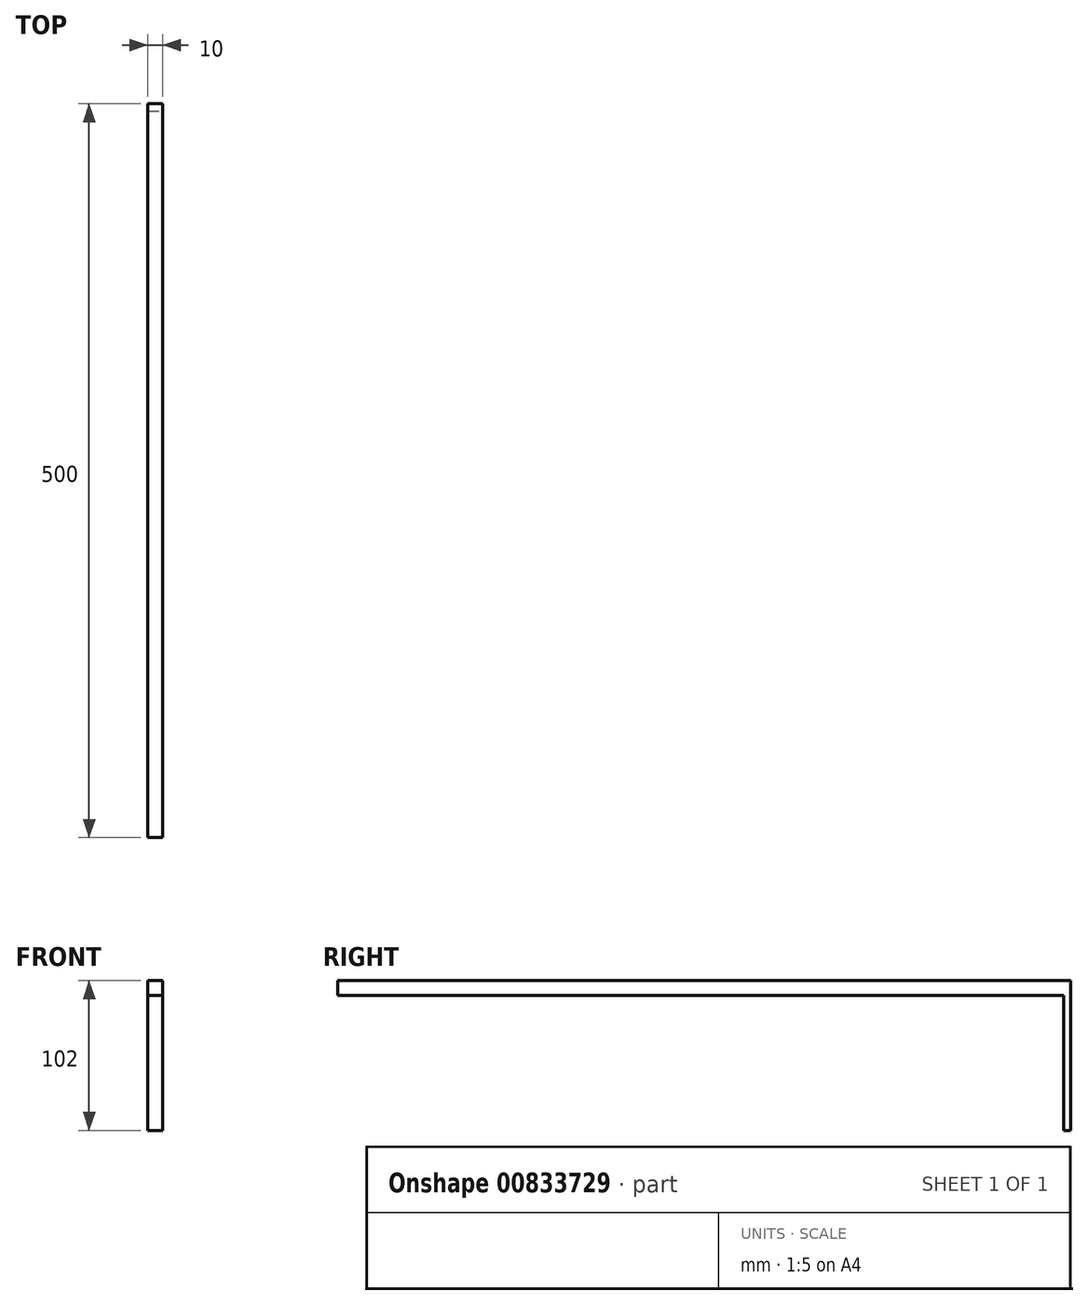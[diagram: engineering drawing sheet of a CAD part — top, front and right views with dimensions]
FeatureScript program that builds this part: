
annotation { "Feature Type Name" : "Feature", "Feature Type Description" : "" }
export const myFeature = defineFeature(function(context is Context, id is Id, definition is map)
    precondition{}
    {
        {
            var Q0;
            Q0=qCreatedBy(makeId("Right.planeOp"),FACE);
            var sketch = newSketch(context, id + "F0", { "sketchPlane" : qUnion([Q0])});
            skLineSegment(sketch, "E0", {"start": v(387.3, 17.23) * mm, "end": v(387.3, -74.77) * mm});
            skLineSegment(sketch, "E1", {"start": v(387.3, 17.23) * mm, "end": v(-112.7, 17.23) * mm});
            skEllipse(sketch, "E2", {"center": v(387.3, 17.23) * mm, "majorRadius": 500 * mm, "minorRadius": 224.74 * mm, "majorAxis": v(-1, 0)});
            skPoint(sketch, "E3.startSnap0", {"position": v(387.3, -207.51) * mm});
            skSolve(sketch);
        }
        {
            var Q0;
            Q0=sQuery(id+"F0.wireOp",EDGE,"E0");
            extrude(context, id + "F1", {"bodyType" : ToolBodyType.SURFACE, "surfaceEntities" : qUnion([Q0]), "depth" : 10 * mm, "offsetDistance" : 25 * mm});
        }
        {
            var Q0;
            Q0=makeQuery(id+"F1.opExtrude","SWEPT_FACE",FACE,{"disambiguationData":[OSD([sQuery(id+"F0.wireOp",EDGE,"E0")])]});
            extrude(context, id + "F2", {"entities" : qUnion([Q0]), "depth" : 5 * mm, "offsetDistance" : 25 * mm});
        }
        {
            var Q0;
            Q0=sQuery(id+"F0.wireOp",EDGE,"E1");
            extrude(context, id + "F3", {"bodyType" : ToolBodyType.SURFACE, "surfaceEntities" : qUnion([Q0]), "depth" : 10 * mm, "offsetDistance" : 25 * mm});
        }
        {
            var Q0;
            Q0=makeQuery(id+"F3.opExtrude","SWEPT_FACE",FACE,{"disambiguationData":[OSD([sQuery(id+"F0.wireOp",EDGE,"E1")])]});
            extrude(context, id + "F4", {"entities" : qUnion([Q0]), "operationType" : NewBodyOperationType.ADD, "depth" : 10 * mm, "offsetDistance" : 25 * mm});
        }
        {
            var Q0;
            Q0=sQuery(id+"F0.wireOp",EDGE,"E2");
            extrude(context, id + "F5", {"bodyType" : ToolBodyType.SURFACE, "surfaceEntities" : qUnion([Q0]), "depth" : 20 * mm, "offsetDistance" : 25 * mm});
        }
    });
